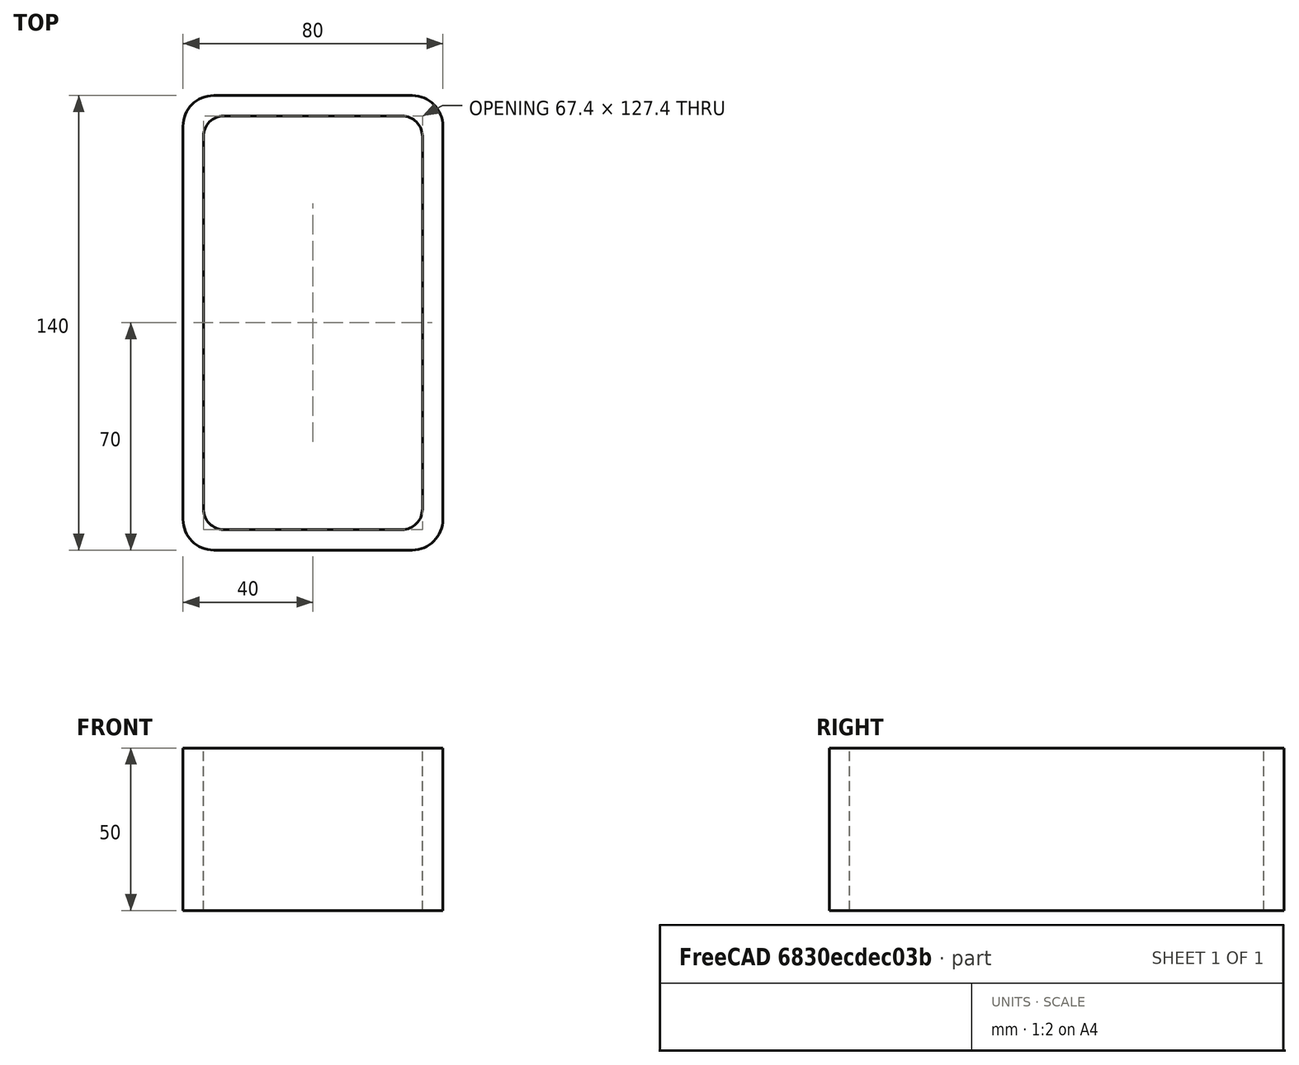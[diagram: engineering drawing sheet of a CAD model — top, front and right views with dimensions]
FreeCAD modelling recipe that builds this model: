
FCSTD DOCUMENT  (FreeCAD 0.15R4671 (Git))
Label: Rectangular hollow section 140x80x6.3 EN10219 S235JRH
License: All rights reserved
LicenseURL: http://en.wikipedia.org/wiki/All_rights_reserved
objects: Sketcher::SketchObject×1, Part::Extrusion×1
note: 2 computed .brp shape members not serialized (recipe doc carries the construction recipe); baked Part::Feature solids carry a one-line shape summary decoded from their .brp

FEATURE [Sketcher::SketchObject] Sketch
  sketch-geometry (16):
    g0: LineSegment StartX=-27.4 StartY=63.7 StartZ=0 EndX=27.4 EndY=63.7 EndZ=0
    g1: LineSegment StartX=33.7 StartY=57.4 StartZ=0 EndX=33.7 EndY=-57.4 EndZ=0
    g2: LineSegment StartX=27.4 StartY=-63.7 StartZ=0 EndX=-27.4 EndY=-63.7 EndZ=0
    g3: LineSegment StartX=-33.7 StartY=-57.4 StartZ=0 EndX=-33.7 EndY=57.4 EndZ=0
    g4: LineSegment StartX=-30.55 StartY=70 StartZ=0 EndX=30.55 EndY=70 EndZ=0
    g5: LineSegment StartX=40 StartY=60.55 StartZ=0 EndX=40 EndY=-60.55 EndZ=0
    g6: LineSegment StartX=30.55 StartY=-70 StartZ=0 EndX=-30.55 EndY=-70 EndZ=0
    g7: LineSegment StartX=-40 StartY=-60.55 StartZ=0 EndX=-40 EndY=60.55 EndZ=0
    g8: ArcOfCircle CenterX=-27.4 CenterY=57.4 CenterZ=0 NormalX=0 NormalY=0 NormalZ=1 Radius=6.3 StartAngle=1.5708 EndAngle=3.14159
    g9: ArcOfCircle CenterX=27.4 CenterY=57.4 CenterZ=0 NormalX=0 NormalY=0 NormalZ=1 Radius=6.3 StartAngle=0 EndAngle=1.5708
    g10: ArcOfCircle CenterX=27.4 CenterY=-57.4 CenterZ=0 NormalX=0 NormalY=0 NormalZ=1 Radius=6.3 StartAngle=4.71239 EndAngle=6.28319
    g11: ArcOfCircle CenterX=-27.4 CenterY=-57.4 CenterZ=0 NormalX=0 NormalY=0 NormalZ=1 Radius=6.3 StartAngle=3.14159 EndAngle=4.71239
    g12: ArcOfCircle CenterX=30.55 CenterY=60.55 CenterZ=0 NormalX=0 NormalY=0 NormalZ=1 Radius=9.45 StartAngle=0 EndAngle=1.5708
    g13: ArcOfCircle CenterX=30.55 CenterY=-60.55 CenterZ=0 NormalX=0 NormalY=0 NormalZ=1 Radius=9.45 StartAngle=4.71239 EndAngle=6.28319
    g14: ArcOfCircle CenterX=-30.55 CenterY=-60.55 CenterZ=0 NormalX=0 NormalY=0 NormalZ=1 Radius=9.45 StartAngle=3.14159 EndAngle=4.71239
    g15: ArcOfCircle CenterX=-30.55 CenterY=60.55 CenterZ=0 NormalX=0 NormalY=0 NormalZ=1 Radius=9.45 StartAngle=1.5708 EndAngle=3.14159
  constraints (36):
    c: Horizontal(g2)
    c: Vertical(g3)
    c: Horizontal(g6)
    c: Vertical(g7)
    c: Tangent(g3,g8) = 1.5708
    c: Tangent(g0,g8) = 1.5708
    c: Tangent(g0,g9) = 1.5708
    c: Tangent(g1,g9) = 1.5708
    c: Tangent(g1,g10) = 1.5708
    c: Tangent(g2,g10) = 1.5708
    c: Tangent(g2,g11) = 1.5708
    c: Tangent(g3,g11) = 1.5708
    c: Tangent(g4,g12) = 1.5708
    c: Tangent(g5,g12) = 1.5708
    c: Tangent(g5,g13) = 1.5708
    c: Tangent(g6,g13) = 1.5708
    c: Tangent(g6,g14) = 1.5708
    c: Tangent(g7,g14) = 1.5708
    c: Tangent(g7,g15) = 1.5708
    c: Tangent(g4,g15) = 1.5708
    c: Equal(g9,g8)
    c: Equal(g9,g11)
    c: Equal(g9,g10)
    c: Equal(g12,g15)
    c: Equal(g12,g14)
    c: Equal(g12,g13)
    c: Symmetric(g4,g6,g-1)
    c: Symmetric(g7,g5,g-2)
    c: DistanceY(g4,g6) = -140
    c: DistanceX(g7,g5) = 80
    c: Symmetric(g3,g1,g-2)
    c: Symmetric(g0,g2,g-1)
    c: DistanceY(g0,g4) = 6.3
    c: DistanceX(g5,g1) = -6.3
    c: Radius(g9) = 6.3
    c: Radius(g12) = 9.45
FEATURE [Part::Extrusion] Extrude  label="Rectangular hollow section 140x80x6.3 EN10219 S235JRH"
  Base = -> Sketch
  Dir = (0,0,50)
  Solid = true
